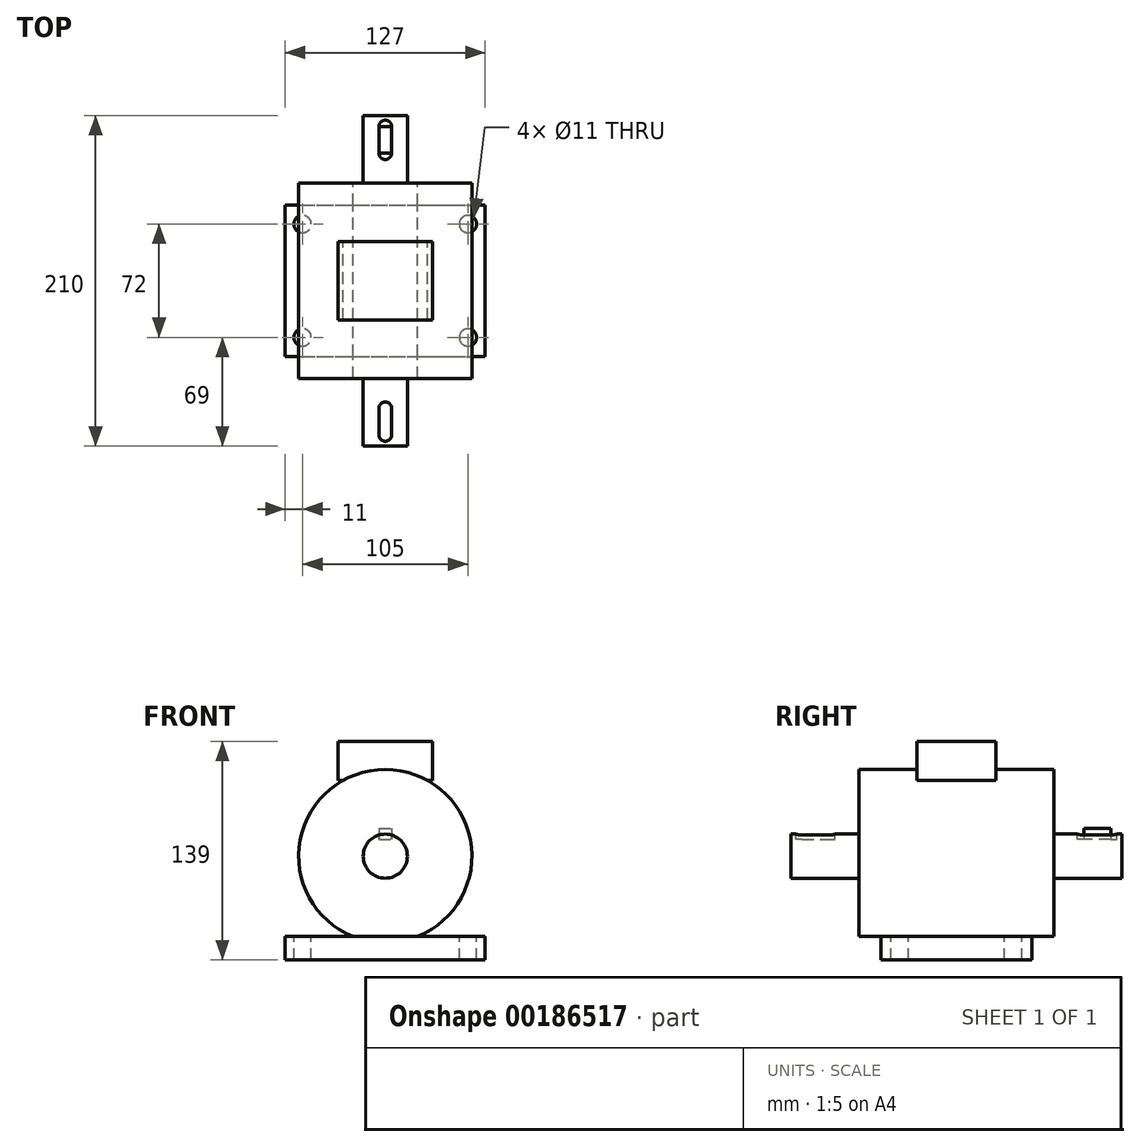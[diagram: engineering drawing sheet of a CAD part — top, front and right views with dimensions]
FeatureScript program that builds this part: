
annotation { "Feature Type Name" : "Feature", "Feature Type Description" : "" }
export const myFeature = defineFeature(function(context is Context, id is Id, definition is map)
    precondition{}
    {
        {
            var Q0;
            Q0=qCreatedBy(makeId("Top.planeOp"),FACE);
            var sketch = newSketch(context, id + "F0", { "sketchPlane" : qUnion([Q0])});
            skLineSegment(sketch, "E0.bottom", {"start": v(-63.5, 48) * mm, "end": v(63.5, 48) * mm});
            skLineSegment(sketch, "E0.top", {"start": v(-63.5, -48) * mm, "end": v(63.5, -48) * mm});
            skLineSegment(sketch, "E0.left", {"start": v(-63.5, 48) * mm, "end": v(-63.5, -48) * mm});
            skLineSegment(sketch, "E0.right", {"start": v(63.5, 48) * mm, "end": v(63.5, -48) * mm});
            skSolve(sketch);
        }
        {
            var Q0;
            Q0=makeQuery(id+"F0.imprint","IMPRINT",FACE,{"disambiguationData":[TD([[makeQuery(id+"F0.imprint","IMPRINT",EDGE,{"derivedFrom":sQuery(id+"F0.wireOp",EDGE,"E0.bottom")}),-1.0]])]});
            extrude(context, id + "F1", {"entities" : qUnion([Q0]), "depth" : 15 * mm});
        }
        {
            var Q0;
            Q0=qCreatedBy(makeId("Front.planeOp"),FACE);
            var sketch = newSketch(context, id + "F2", { "sketchPlane" : qUnion([Q0])});
            skArc(sketch, "E1", {"start": v(20.6, 15) * mm, "mid": v(0, 121) * mm, "end": v(-20.6, 15) * mm});
            skLineSegment(sketch, "E2.0", {"start": v(-20.6, 15) * mm, "end": v(20.6, 15) * mm});
            skPoint(sketch, "E3.orphan", {"position": v(63.5, 15) * mm});
            skPoint(sketch, "E4.orphan", {"position": v(-63.5, 15) * mm});
            skSolve(sketch);
        }
        {
            var Q0;
            Q0=makeQuery(id+"F2.imprint","IMPRINT",FACE,{"disambiguationData":[TD([[makeQuery(id+"F2.imprint","IMPRINT",EDGE,{"derivedFrom":sQuery(id+"F2.wireOp",EDGE,"E1")}),1.0]])]});
            extrude(context, id + "F3", {"entities" : qUnion([Q0]), "operationType" : NewBodyOperationType.ADD, "depth" : 62 * mm, "hasSecondDirection" : true, "secondDirectionOppositeDirection" : true, "secondDirectionDepth" : 62 * mm});
        }
        {
            var Q0;
            Q0=makeQuery(id+"F3.opExtrude","CAP_FACE",FACE,{"disambiguationData":[OSD([sQuery(id+"F2.wireOp",EDGE,"E1")])],"isStart":true});
            var sketch = newSketch(context, id + "F4", { "sketchPlane" : qUnion([Q0])});
            skCircle(sketch, "E5", {"center": v(0, 66) * mm, "radius": 14 * mm});
            skSolve(sketch);
        }
        {
            var Q0;
            Q0=makeQuery(id+"F4.imprint","IMPRINT",FACE,{"disambiguationData":[TD([[makeQuery(id+"F4.imprint","IMPRINT",EDGE,{"derivedFrom":sQuery(id+"F4.wireOp",EDGE,"E5")}),1.0]])]});
            extrude(context, id + "F5", {"entities" : qUnion([Q0]), "operationType" : NewBodyOperationType.ADD, "depth" : 43 * mm});
        }
        {
            var Q0;
            Q0=makeQuery(id+"F3.opExtrude","CAP_FACE",FACE,{"disambiguationData":[OSD([sQuery(id+"F2.wireOp",EDGE,"E1")])],"isStart":false});
            var sketch = newSketch(context, id + "F6", { "sketchPlane" : qUnion([Q0])});
            skCircle(sketch, "E6", {"center": v(0, 66) * mm, "radius": 14 * mm});
            skSolve(sketch);
        }
        {
            var Q0;
            Q0=makeQuery(id+"F6.imprint","IMPRINT",FACE,{"disambiguationData":[TD([[makeQuery(id+"F6.imprint","IMPRINT",EDGE,{"derivedFrom":sQuery(id+"F6.wireOp",EDGE,"E6")}),1.0]])]});
            extrude(context, id + "F7", {"entities" : qUnion([Q0]), "operationType" : NewBodyOperationType.ADD, "depth" : 43 * mm});
        }
        {
            var Q0;
            Q0=qCreatedBy(makeId("Top.planeOp"),FACE);
            cPlane(context, id + "F8", {"entities" : qUnion([Q0]), "cplaneType" : CPlaneType.OFFSET, "offset" : 80 * mm, "width" : 150 * mm, "height" : 150 * mm});
        }
        {
            var Q0;
            Q0=qCreatedBy(id+"F8.planeOp",FACE);
            var sketch = newSketch(context, id + "F9", { "sketchPlane" : qUnion([Q0])});
            skLineSegment(sketch, "E7.left", {"start": v(-4, 98) * mm, "end": v(-4, 81) * mm});
            skLineSegment(sketch, "E7.right", {"start": v(4, 98) * mm, "end": v(4, 81) * mm});
            skArc(sketch, "E8", {"start": v(4, 98) * mm, "mid": v(0, 102) * mm, "end": v(-4, 98) * mm});
            skArc(sketch, "E9", {"start": v(-4, 81) * mm, "mid": v(0, 77) * mm, "end": v(4, 81) * mm});
            skPoint(sketch, "E9.centerSnap0", {"position": v(0, 75) * mm});
            skPoint(sketch, "E10.orphan", {"position": v(-4, 75) * mm});
            skPoint(sketch, "E11.orphan", {"position": v(4, 75) * mm});
            skArc(sketch, "E12.MirrorCS", {"start": v(-4, -81) * mm, "mid": v(0, -77) * mm, "end": v(4, -81) * mm});
            skArc(sketch, "E13.MirrorCS", {"start": v(4, -98) * mm, "mid": v(0, -102) * mm, "end": v(-4, -98) * mm});
            skLineSegment(sketch, "E14.MirrorCS", {"start": v(-4, -98) * mm, "end": v(-4, -81) * mm});
            skLineSegment(sketch, "E15.MirrorCS", {"start": v(4, -98) * mm, "end": v(4, -81) * mm});
            skPoint(sketch, "E16.MirrorP", {"position": v(-4, -75) * mm});
            skPoint(sketch, "E17.MirrorP", {"position": v(0, -75) * mm});
            skPoint(sketch, "E18.MirrorP", {"position": v(4, -75) * mm});
            skSolve(sketch);
        }
        {
            var Q0;
            Q0 = qSketchRegion(id + "F9", true);
            extrude(context, id + "F10", {"entities" : qUnion([Q0]), "operationType" : NewBodyOperationType.REMOVE, "oppositeDirection" : true, "depth" : 3.5 * mm});
        }
        {
            var Q0;
            Q0=makeQuery(id+"F1.opExtrude","CAP_FACE",FACE,{"disambiguationData":[OSD([sQuery(id+"F0.wireOp",EDGE,"E0.bottom"),sQuery(id+"F0.wireOp",EDGE,"E0.top"),sQuery(id+"F0.wireOp",EDGE,"E0.left"),sQuery(id+"F0.wireOp",EDGE,"E0.right")])],"isStart":false});
            var sketch = newSketch(context, id + "F11", { "sketchPlane" : qUnion([Q0])});
            skPoint(sketch, "E19", {"position": v(-52.5, 36) * mm});
            skPoint(sketch, "E20", {"position": v(52.5, 36) * mm});
            skPoint(sketch, "E21", {"position": v(52.5, -36) * mm});
            skPoint(sketch, "E22", {"position": v(-52.5, -36) * mm});
            skSolve(sketch);
        }
        {
            var Q0;
            Q0=sQuery(id+"F11.wireOp",VERTEX,"E20");
            var Q1;
            Q1=sQuery(id+"F11.wireOp",VERTEX,"E21");
            var Q2;
            Q2=sQuery(id+"F11.wireOp",VERTEX,"E22");
            var Q3;
            Q3=sQuery(id+"F11.wireOp",VERTEX,"E19");
            var Q4;
            Q4=makeQuery(id+"F1.opExtrude","SWEPT_BODY",BODY,{"disambiguationData":[OSD([sQuery(id+"F0.wireOp",EDGE,"E0.bottom"),sQuery(id+"F0.wireOp",EDGE,"E0.top"),sQuery(id+"F0.wireOp",EDGE,"E0.left"),sQuery(id+"F0.wireOp",EDGE,"E0.right")])]});
            hole(context, id + "F12", {"style" : HoleStyle.SIMPLE, "endStyle" : HoleEndStyle.THROUGH, "standardTappedOrClearance" : lookupTablePath({ "standard" : "ISO", "size" : "11", "type" : "Drilled" }), "standardBlindInLast" : lookupTablePath({ "standard" : "ISO", "size" : "11", "type" : "Drilled" }), "holeDiameter" : 11 * mm, "locations" : qUnion([Q0, Q1, Q2, Q3]), "scope" : qUnion([Q4]), "isTappedThrough" : true});
        }
        {
            var Q0;
            Q0=qCreatedBy(makeId("Front.planeOp"),FACE);
            var sketch = newSketch(context, id + "F13", { "sketchPlane" : qUnion([Q0])});
            skLineSegment(sketch, "E23.bottom", {"start": v(-30, 139) * mm, "end": v(30, 139) * mm});
            skLineSegment(sketch, "E23.top", {"start": v(-30, 114) * mm, "end": v(-26.85, 114) * mm});
            skLineSegment(sketch, "E23.left", {"start": v(-30, 139) * mm, "end": v(-30, 114) * mm});
            skLineSegment(sketch, "E23.right", {"start": v(30, 139) * mm, "end": v(30, 114) * mm});
            skArc(sketch, "E24.0", {"start": v(26.85, 114) * mm, "mid": v(0, 121) * mm, "end": v(-26.85, 114) * mm});
            skPoint(sketch, "E25.orphan", {"position": v(20.6, 15) * mm});
            skLineSegment(sketch, "E26.trimOffspring", {"start": v(26.85, 114) * mm, "end": v(30, 114) * mm});
            skPoint(sketch, "E27.orphan", {"position": v(-20.6, 15) * mm});
            skSolve(sketch);
        }
        {
            var Q0;
            Q0=makeQuery(id+"F13.imprint","IMPRINT",FACE,{"disambiguationData":[TD([[makeQuery(id+"F13.imprint","IMPRINT",EDGE,{"derivedFrom":sQuery(id+"F13.wireOp",EDGE,"E23.bottom")}),-1.0]])]});
            extrude(context, id + "F14", {"entities" : qUnion([Q0]), "operationType" : NewBodyOperationType.ADD, "depth" : 25 * mm, "hasSecondDirection" : true, "secondDirectionOppositeDirection" : true, "secondDirectionDepth" : 25 * mm});
        }
        {
            var Q0;
            Q0=makeQuery(id+"F10.boolean.opBoolean","COPY",FACE,{"derivedFrom":makeQuery(id+"F10.opExtrude","CAP_FACE",FACE,{"disambiguationData":[OSD([sQuery(id+"F9.wireOp",EDGE,"E7.left"),sQuery(id+"F9.wireOp",EDGE,"E7.right"),sQuery(id+"F9.wireOp",EDGE,"E8"),sQuery(id+"F9.wireOp",EDGE,"E9")])],"isStart":false})});
            var sketch = newSketch(context, id + "F15", { "sketchPlane" : qUnion([Q0])});
            skLineSegment(sketch, "E28.bottom", {"start": v(-4, 98) * mm, "end": v(4, 98) * mm});
            skLineSegment(sketch, "E28.top", {"start": v(-4, 81) * mm, "end": v(4, 81) * mm});
            skLineSegment(sketch, "E28.left", {"start": v(-4, 98) * mm, "end": v(-4, 81) * mm});
            skLineSegment(sketch, "E28.right", {"start": v(4, 98) * mm, "end": v(4, 81) * mm});
            skSolve(sketch);
        }
        {
            var Q0;
            Q0=makeQuery(id+"F15.imprint","IMPRINT",FACE,{"disambiguationData":[TD([[makeQuery(id+"F15.imprint","IMPRINT",EDGE,{"derivedFrom":sQuery(id+"F15.wireOp",EDGE,"E28.bottom")}),-1.0]])]});
            extrude(context, id + "F16", {"entities" : qUnion([Q0]), "depth" : 7 * mm});
        }
        {
            var Q0;
            Q0=makeQuery(id+"F10.boolean.opBoolean","COPY",FACE,{"derivedFrom":makeQuery(id+"F10.opExtrude","CAP_FACE",FACE,{"disambiguationData":[OSD([sQuery(id+"F9.wireOp",EDGE,"E12.MirrorCS"),sQuery(id+"F9.wireOp",EDGE,"E13.MirrorCS"),sQuery(id+"F9.wireOp",EDGE,"E14.MirrorCS"),sQuery(id+"F9.wireOp",EDGE,"E15.MirrorCS")])],"isStart":false})});
            var sketch = newSketch(context, id + "F17", { "sketchPlane" : qUnion([Q0])});
            skLineSegment(sketch, "E29.bottom", {"start": v(-4, -81) * mm, "end": v(4, -81) * mm});
            skLineSegment(sketch, "E29.top", {"start": v(-4, -98) * mm, "end": v(4, -98) * mm});
            skLineSegment(sketch, "E29.left", {"start": v(-4, -81) * mm, "end": v(-4, -98) * mm});
            skLineSegment(sketch, "E29.right", {"start": v(4, -81) * mm, "end": v(4, -98) * mm});
            skSolve(sketch);
        }
        {
            var Q0;
            Q0=makeQuery(id+"F17.imprint","IMPRINT",FACE,{"disambiguationData":[TD([[makeQuery(id+"F17.imprint","IMPRINT",EDGE,{"derivedFrom":sQuery(id+"F17.wireOp",EDGE,"E29.bottom")}),-1.0]])]});
            extrude(context, id + "F18", {"entities" : qUnion([Q0]), "depth" : 7 * mm});
        }
        {
            var Q0;
            Q0=makeQuery(id+"F18.opExtrude","SWEPT_BODY",BODY,{"disambiguationData":[OSD([sQuery(id+"F17.wireOp",EDGE,"E29.bottom"),sQuery(id+"F17.wireOp",EDGE,"E29.top"),sQuery(id+"F17.wireOp",EDGE,"E29.left"),sQuery(id+"F17.wireOp",EDGE,"E29.right")])]});
            deleteBodies(context, id + "F19", {"entities" : qUnion([Q0])});
        }
    });
